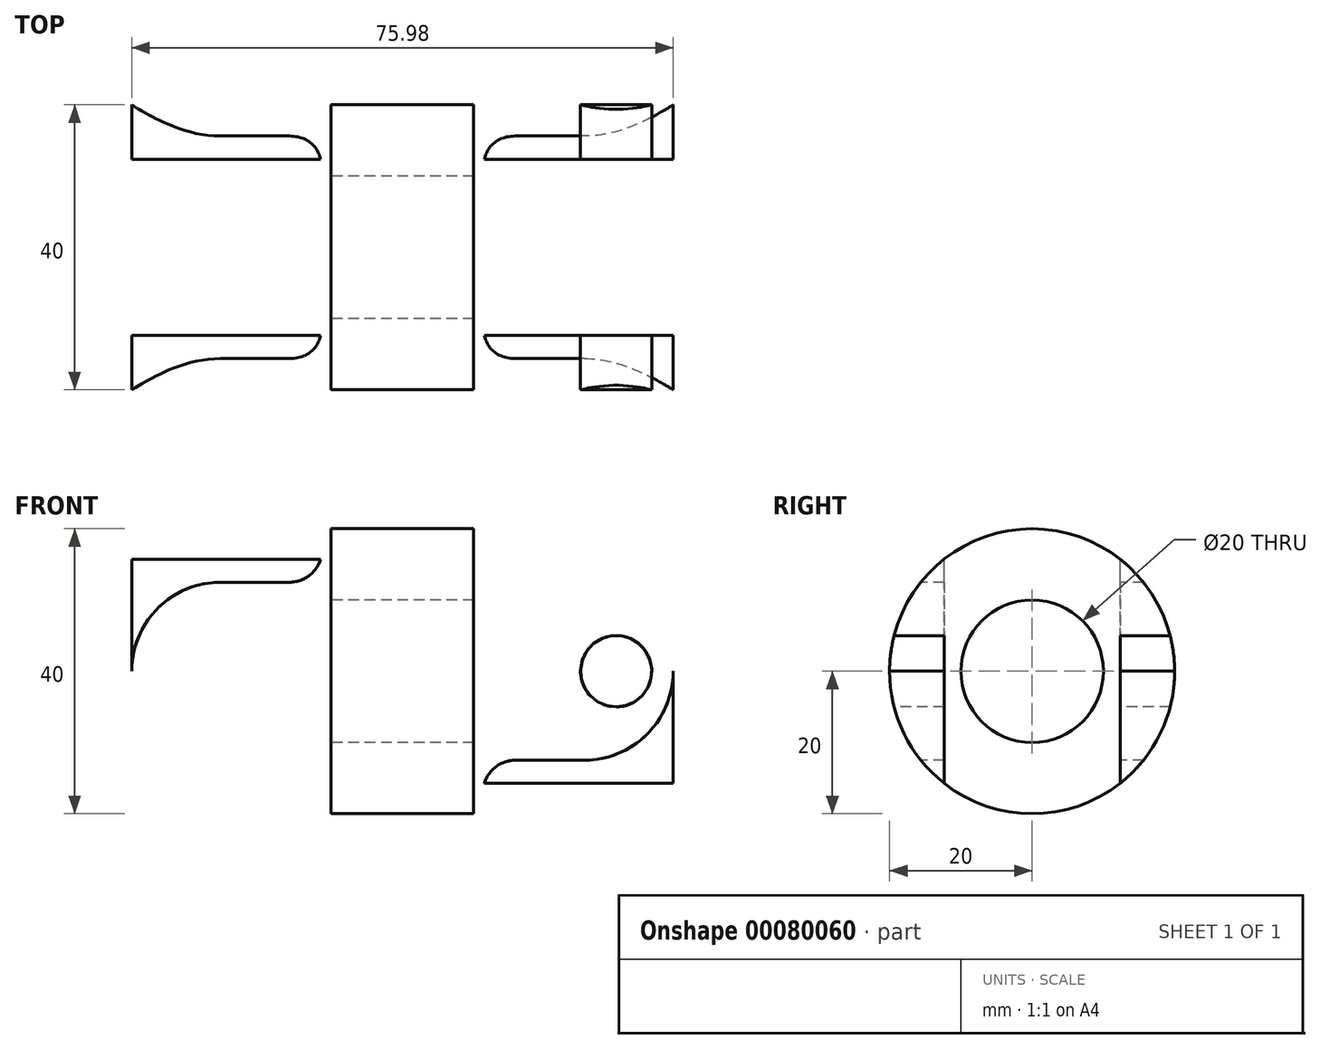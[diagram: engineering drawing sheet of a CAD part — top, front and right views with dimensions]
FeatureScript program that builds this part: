
annotation { "Feature Type Name" : "Feature", "Feature Type Description" : "" }
export const myFeature = defineFeature(function(context is Context, id is Id, definition is map)
    precondition{}
    {
        {
            var Q0;
            Q0=qCreatedBy(makeId("Front.planeOp"),FACE);
            var sketch = newSketch(context, id + "F0", { "sketchPlane" : qUnion([Q0])});
            skLineSegment(sketch, "E0.bottom", {"start": v(-38, 20) * mm, "end": v(38, 20) * mm});
            skLineSegment(sketch, "E0.top", {"start": v(-38, 10) * mm, "end": v(38, 10) * mm});
            skLineSegment(sketch, "E0.left", {"start": v(-38, 20) * mm, "end": v(-38, 10) * mm});
            skLineSegment(sketch, "E0.right", {"start": v(38, 20) * mm, "end": v(38, 10) * mm});
            skLineSegment(sketch, "E1", {"start": v(-83.5, 0) * mm, "end": v(81.07, 0) * mm, "construction": true});
            skSolve(sketch);
        }
        {
            var Q0;
            Q0=makeQuery(id+"F0.imprint","IMPRINT",FACE,{"disambiguationData":[TD([[makeQuery(id+"F0.imprint","IMPRINT",EDGE,{"derivedFrom":sQuery(id+"F0.wireOp",EDGE,"E0.bottom")}),-1.0]])]});
            var Q1;
            Q1=sQuery(id+"F0.wireOp",EDGE,"E1");
            revolve(context, id + "F1", {"entities" : qUnion([Q0]), "axis" : qUnion([Q1]), "revolveType" : RevolveType.FULL});
        }
        {
            var Q0;
            Q0=qCreatedBy(makeId("Top.planeOp"),FACE);
            var sketch = newSketch(context, id + "F2", { "sketchPlane" : qUnion([Q0])});
            skLineSegment(sketch, "E2.bottom", {"start": v(-38, 12.36) * mm, "end": v(-10, 12.36) * mm});
            skLineSegment(sketch, "E2.top", {"start": v(-38, -12.36) * mm, "end": v(-10, -12.36) * mm});
            skLineSegment(sketch, "E2.left", {"start": v(-38, 12.36) * mm, "end": v(-38, -12.36) * mm});
            skLineSegment(sketch, "E2.right", {"start": v(-10, 12.36) * mm, "end": v(-10, -12.36) * mm});
            skLineSegment(sketch, "E3.bottom", {"start": v(38, 12.36) * mm, "end": v(10, 12.36) * mm});
            skLineSegment(sketch, "E3.top", {"start": v(38, -12.36) * mm, "end": v(10, -12.36) * mm});
            skLineSegment(sketch, "E3.left", {"start": v(38, 12.36) * mm, "end": v(38, -12.36) * mm});
            skLineSegment(sketch, "E3.right", {"start": v(10, 12.36) * mm, "end": v(10, -12.36) * mm});
            skLineSegment(sketch, "E4", {"start": v(-48.23, 0) * mm, "end": v(65.3, 0) * mm});
            skSolve(sketch);
        }
        {
            var Q0;
            Q0 = qSketchRegion(id + "F2", true);
            extrude(context, id + "F3", {"entities" : qUnion([Q0]), "operationType" : NewBodyOperationType.REMOVE, "endBound" : BoundingType.THROUGH_ALL, "oppositeDirection" : true, "depth" : 25 * mm, "hasSecondDirection" : true, "secondDirectionBound" : SecondDirectionBoundingType.THROUGH_ALL, "secondDirectionOppositeDirection" : false, "secondDirectionDepth" : 25 * mm});
        }
        {
            var Q0;
            Q0=qCreatedBy(makeId("Front.planeOp"),FACE);
            var sketch = newSketch(context, id + "F4", { "sketchPlane" : qUnion([Q0])});
            skLineSegment(sketch, "E5", {"start": v(0, 0) * mm, "end": v(-92.84, 0) * mm, "construction": true});
            skLineSegment(sketch, "E6", {"start": v(-38, 29.25) * mm, "end": v(-37.99, -31.01) * mm, "construction": true});
            skArc(sketch, "E7", {"start": v(-38, 0) * mm, "mid": v(-34.33, -8.84) * mm, "end": v(-25.5, -12.5) * mm});
            skLineSegment(sketch, "E8", {"start": v(-25.5, -12.5) * mm, "end": v(-15.82, -12.5) * mm});
            skPoint(sketch, "E8.endSnap0", {"position": v(-25.5, -12.5) * mm});
            skLineSegment(sketch, "E9", {"start": v(-10, -15.72) * mm, "end": v(-11.5, -15.72) * mm});
            skArc(sketch, "E10", {"start": v(-11.5, -15.72) * mm, "mid": v(-13.12, -13.4) * mm, "end": v(-15.82, -12.5) * mm});
            skPoint(sketch, "E11.orphan", {"position": v(-12.08, -12.5) * mm});
            skLineSegment(sketch, "E12.MirrorCS", {"start": v(-10, 15.72) * mm, "end": v(-11.5, 15.72) * mm});
            skArc(sketch, "E13.MirrorCS", {"start": v(-11.5, 15.72) * mm, "mid": v(-13.12, 13.4) * mm, "end": v(-15.82, 12.5) * mm});
            skArc(sketch, "E14.MirrorCS", {"start": v(-38, 0) * mm, "mid": v(-34.33, 8.84) * mm, "end": v(-25.5, 12.5) * mm});
            skPoint(sketch, "E15.MirrorP", {"position": v(-12.08, 12.5) * mm});
            skPoint(sketch, "E16.MirrorP", {"position": v(-25.5, 12.5) * mm});
            skLineSegment(sketch, "E17.MirrorCS", {"start": v(-25.5, 12.5) * mm, "end": v(-15.82, 12.5) * mm});
            skLineSegment(sketch, "E18", {"start": v(-10, 15.72) * mm, "end": v(-10, -15.72) * mm});
            skLineSegment(sketch, "E19", {"start": v(-11.5, 15.72) * mm, "end": v(-38, 15.72) * mm});
            skLineSegment(sketch, "E20", {"start": v(-38, 15.72) * mm, "end": v(-38, -15.9) * mm});
            skLineSegment(sketch, "E21", {"start": v(-38, -15.9) * mm, "end": v(-11.5, -15.72) * mm});
            skCircle(sketch, "E22", {"center": v(-30, 0) * mm, "radius": 5 * mm});
            skArc(sketch, "E23.MirrorCS", {"start": v(11.5, 15.72) * mm, "mid": v(13.12, 13.4) * mm, "end": v(15.82, 12.5) * mm});
            skLineSegment(sketch, "E24.MirrorCS", {"start": v(10, 15.72) * mm, "end": v(11.5, 15.72) * mm});
            skArc(sketch, "E25.MirrorCS", {"start": v(11.5, -15.72) * mm, "mid": v(13.12, -13.4) * mm, "end": v(15.82, -12.5) * mm});
            skLineSegment(sketch, "E26.MirrorCS", {"start": v(10, -15.72) * mm, "end": v(11.5, -15.72) * mm});
            skLineSegment(sketch, "E27.MirrorCS", {"start": v(10, 15.72) * mm, "end": v(10, -15.72) * mm});
            skLineSegment(sketch, "E28.MirrorCS", {"start": v(25.5, 12.5) * mm, "end": v(15.82, 12.5) * mm});
            skLineSegment(sketch, "E29.MirrorCS", {"start": v(25.5, -12.5) * mm, "end": v(15.82, -12.5) * mm});
            skLineSegment(sketch, "E30.MirrorCS", {"start": v(38, 15.72) * mm, "end": v(38, -15.9) * mm});
            skLineSegment(sketch, "E31.MirrorCS", {"start": v(11.5, 15.72) * mm, "end": v(38, 15.72) * mm});
            skArc(sketch, "E32.MirrorCS", {"start": v(38, 0) * mm, "mid": v(34.33, 8.84) * mm, "end": v(25.5, 12.5) * mm});
            skArc(sketch, "E33.MirrorCS", {"start": v(38, 0) * mm, "mid": v(34.33, -8.84) * mm, "end": v(25.5, -12.5) * mm});
            skCircle(sketch, "E34.MirrorC", {"center": v(30, 0) * mm, "radius": 5 * mm});
            skLineSegment(sketch, "E35.MirrorCS", {"start": v(38, -15.9) * mm, "end": v(11.5, -15.72) * mm});
            skLineSegment(sketch, "E36.MirrorCS", {"start": v(38, 29.25) * mm, "end": v(37.99, -31.01) * mm, "construction": true});
            skPoint(sketch, "E37.MirrorP", {"position": v(12.08, 12.5) * mm});
            skPoint(sketch, "E38.MirrorP", {"position": v(25.5, -12.5) * mm});
            skPoint(sketch, "E39.MirrorP", {"position": v(12.08, -12.5) * mm});
            skLineSegment(sketch, "E40.MirrorCS", {"start": v(0, 0) * mm, "end": v(92.84, 0) * mm, "construction": true});
            skPoint(sketch, "E41.MirrorP", {"position": v(25.5, 12.5) * mm});
            skSolve(sketch);
        }
        {
            var Q0;
            Q0=makeQuery(id+"F4.imprint","IMPRINT",FACE,{"disambiguationData":[TD([[makeQuery(id+"F4.imprint","IMPRINT",EDGE,{"derivedFrom":sQuery(id+"F4.wireOp",EDGE,"E13.MirrorCS")}),-1.0]])]});
            var Q1;
            {var subQ1=sQuery(id+"F4.wireOp",EDGE,"E7");Q1=makeQuery(id+"F4.imprint","IMPRINT",FACE,{"disambiguationData":[TD([[makeQuery(id+"F4.imprint","IMPRINT",EDGE,{"derivedFrom":subQ1}),-1.0]])]});}
            var Q2;
            Q2=makeQuery(id+"F4.imprint","IMPRINT",FACE,{"disambiguationData":[TD([[makeQuery(id+"F4.imprint","IMPRINT",EDGE,{"derivedFrom":sQuery(id+"F4.wireOp",EDGE,"E22")}),1.0]])]});
            var Q3;
            Q3=makeQuery(id+"F4.imprint","IMPRINT",FACE,{"disambiguationData":[TD([[makeQuery(id+"F4.imprint","IMPRINT",EDGE,{"derivedFrom":sQuery(id+"F4.wireOp",EDGE,"E34.MirrorC")}),-1.0]])]});
            var Q4;
            Q4=makeQuery(id+"F4.imprint","IMPRINT",FACE,{"disambiguationData":[TD([[makeQuery(id+"F4.imprint","IMPRINT",EDGE,{"derivedFrom":sQuery(id+"F4.wireOp",EDGE,"E25.MirrorCS")}),-1.0]])]});
            var Q5;
            Q5=makeQuery(id+"F4.imprint","IMPRINT",FACE,{"disambiguationData":[TD([[makeQuery(id+"F4.imprint","IMPRINT",EDGE,{"derivedFrom":sQuery(id+"F4.wireOp",EDGE,"E23.MirrorCS")}),1.0]])]});
            extrude(context, id + "F5", {"entities" : qUnion([Q0, Q1, Q2, Q3, Q4, Q5]), "operationType" : NewBodyOperationType.REMOVE, "endBound" : BoundingType.THROUGH_ALL, "oppositeDirection" : true, "depth" : 25 * mm, "hasSecondDirection" : true, "secondDirectionBound" : SecondDirectionBoundingType.THROUGH_ALL, "secondDirectionOppositeDirection" : false, "secondDirectionDepth" : 25 * mm});
        }
    });
